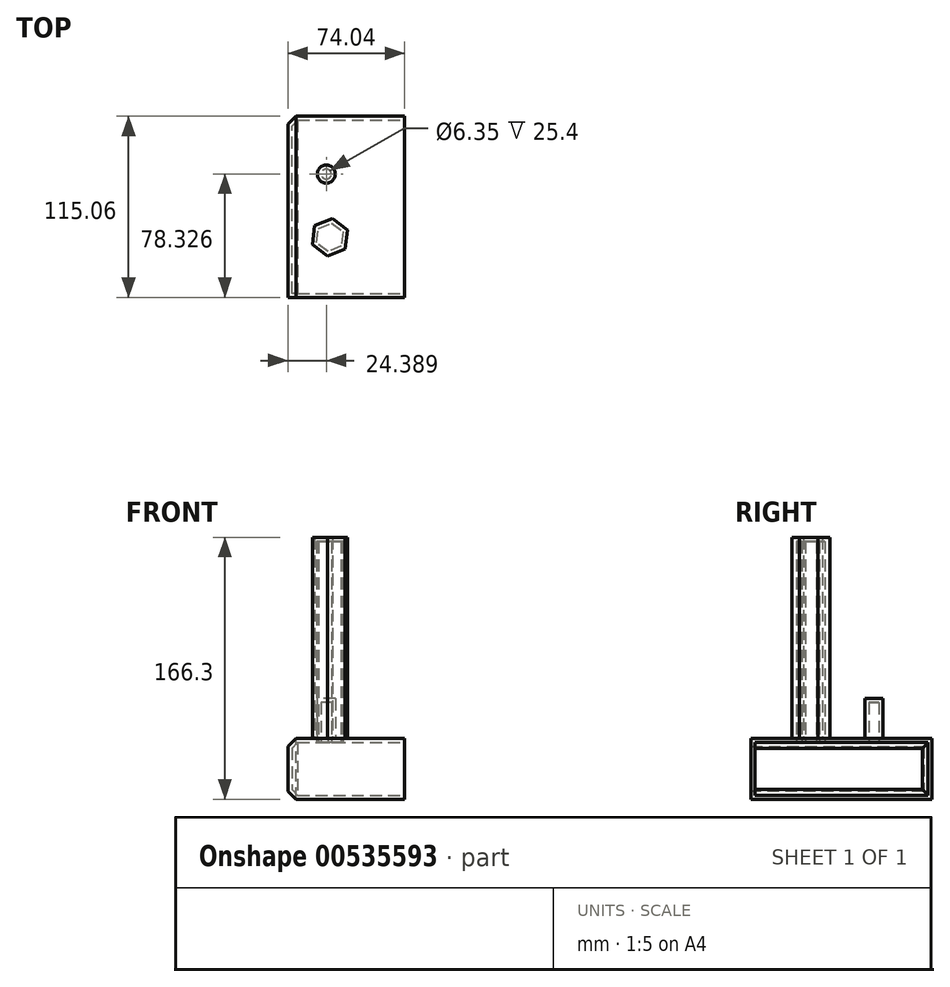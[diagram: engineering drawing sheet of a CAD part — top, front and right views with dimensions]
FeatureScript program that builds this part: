
annotation { "Feature Type Name" : "Feature", "Feature Type Description" : "" }
export const myFeature = defineFeature(function(context is Context, id is Id, definition is map)
    precondition{}
    {
        {
            var Q0;
            Q0=qCreatedBy(makeId("Front.planeOp"),FACE);
            var sketch = newSketch(context, id + "F0", { "sketchPlane" : qUnion([Q0])});
            skLineSegment(sketch, "E0.bottom", {"start": v(-57.8, 38.54) * mm, "end": v(16.24, 38.54) * mm});
            skLineSegment(sketch, "E0.top", {"start": v(-57.8, 0) * mm, "end": v(16.24, 0) * mm});
            skLineSegment(sketch, "E0.left", {"start": v(-57.8, 38.54) * mm, "end": v(-57.8, 0) * mm});
            skLineSegment(sketch, "E0.right", {"start": v(16.24, 38.54) * mm, "end": v(16.24, 0) * mm});
            skSolve(sketch);
        }
        {
            var Q0;
            Q0 = qSketchRegion(id + "F0", true);
            extrude(context, id + "F1", {"entities" : qUnion([Q0]), "depth" : 115.06 * mm, "offsetDistance" : 25.4 * mm});
        }
        {
            var Q0;
            Q0=makeQuery(id+"F1.opExtrude","SWEPT_FACE",FACE,{"disambiguationData":[OSD([sQuery(id+"F0.wireOp",EDGE,"E0.bottom")])]});
            var sketch = newSketch(context, id + "F2", { "sketchPlane" : qUnion([Q0])});
            skCircle(sketch, "E1.cCircle", {"center": v(-31.14, -76.88) * mm, "radius": 10.45 * mm, "construction": true});
            skLineSegment(sketch, "E1.0", {"start": v(-32.7, -88.85) * mm, "end": v(-42.29, -81.51) * mm});
            skLineSegment(sketch, "E1.1", {"start": v(-42.29, -81.51) * mm, "end": v(-40.73, -69.54) * mm});
            skLineSegment(sketch, "E1.2", {"start": v(-40.73, -69.54) * mm, "end": v(-29.58, -64.91) * mm});
            skLineSegment(sketch, "E1.3", {"start": v(-29.58, -64.91) * mm, "end": v(-20, -72.25) * mm});
            skLineSegment(sketch, "E1.4", {"start": v(-20, -72.25) * mm, "end": v(-21.56, -84.22) * mm});
            skLineSegment(sketch, "E1.5", {"start": v(-21.56, -84.22) * mm, "end": v(-32.7, -88.85) * mm});
            skPoint(sketch, "E1.0.midPoint", {"position": v(-37.5, -85.18) * mm});
            skSolve(sketch);
        }
        {
            var Q0;
            Q0 = qSketchRegion(id + "F2", true);
            extrude(context, id + "F3", {"entities" : qUnion([Q0]), "operationType" : NewBodyOperationType.ADD, "depth" : 127.76 * mm, "offsetDistance" : 25.4 * mm});
        }
        {
            var Q0;
            Q0=makeQuery(id+"F1.opExtrude","SWEPT_FACE",FACE,{"disambiguationData":[OSD([sQuery(id+"F0.wireOp",EDGE,"E0.bottom")])]});
            var sketch = newSketch(context, id + "F4", { "sketchPlane" : qUnion([Q0])});
            skCircle(sketch, "E2", {"center": v(-33.41, -36.73) * mm, "radius": 5.72 * mm});
            skSolve(sketch);
        }
        {
            var Q0;
            Q0 = qSketchRegion(id + "F4", true);
            extrude(context, id + "F5", {"entities" : qUnion([Q0]), "operationType" : NewBodyOperationType.ADD, "depth" : 25.4 * mm, "offsetDistance" : 25.4 * mm});
        }
        {
            var Q0;
            Q0=makeQuery(id+"F1.opExtrude","SWEPT_EDGE",EDGE,{"disambiguationData":[OSD([sQuery(id+"F0.wireOp",EDGE,"E0.top"),sQuery(id+"F0.wireOp",EDGE,"E0.left")])]});
            var Q1;
            Q1=makeQuery(id+"F1.opExtrude","CAP_EDGE",EDGE,{"disambiguationData":[OSD([sQuery(id+"F0.wireOp",EDGE,"E0.left")])],"isStart":true});
            chamfer(context, id + "F6", {"entities" : qUnion([Q0, Q1]), "width" : 5.08 * mm, "tangentPropagation" : true});
        }
        {
            var Q0;
            Q0=makeQuery(id+"F1.opExtrude","SWEPT_EDGE",EDGE,{"disambiguationData":[OSD([sQuery(id+"F0.wireOp",EDGE,"E0.bottom"),sQuery(id+"F0.wireOp",EDGE,"E0.left")])]});
            chamfer(context, id + "F7", {"entities" : qUnion([Q0]), "width" : 5.08 * mm, "tangentPropagation" : true});
        }
        {
            var Q0;
            Q0=makeQuery(id+"F1.opExtrude","SWEPT_FACE",FACE,{"disambiguationData":[OSD([sQuery(id+"F0.wireOp",EDGE,"E0.right")])]});
            shell(context, id + "F8", {"entities" : qUnion([Q0]), "thickness" : 2.54 * mm});
        }
    });
